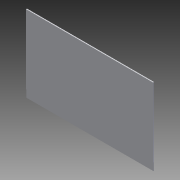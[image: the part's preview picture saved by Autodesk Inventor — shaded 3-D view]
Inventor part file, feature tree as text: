
AUTODESK INVENTOR PART (.ipt)
format: ipt  version: 2012 (Build 160160000, 160)  size: 72,192 bytes
history: native  units: in
note: dims shown in document units (in); Inventor stores cm internally (conversion verified against a paired STEP export)
features: extrude x2, sketch x1
ambient origin geometry x8: Origin, YZ Plane, XZ Plane, XY Plane, X Axis, Y Axis, Z Axis, Center Point
bodies: Solid1 (feature_tree)
feature tree (3):
  sketch  "Sketch1"  dims[d0=20.0in d1=33.0in d2=2.0in d3=0.25in d4=0.0in d5=0.125in d6=0.0in]
  extrude  "Extrusion1"  Depth=33.0in
  extrude  "Extrusion2"  Depth=2.0in
